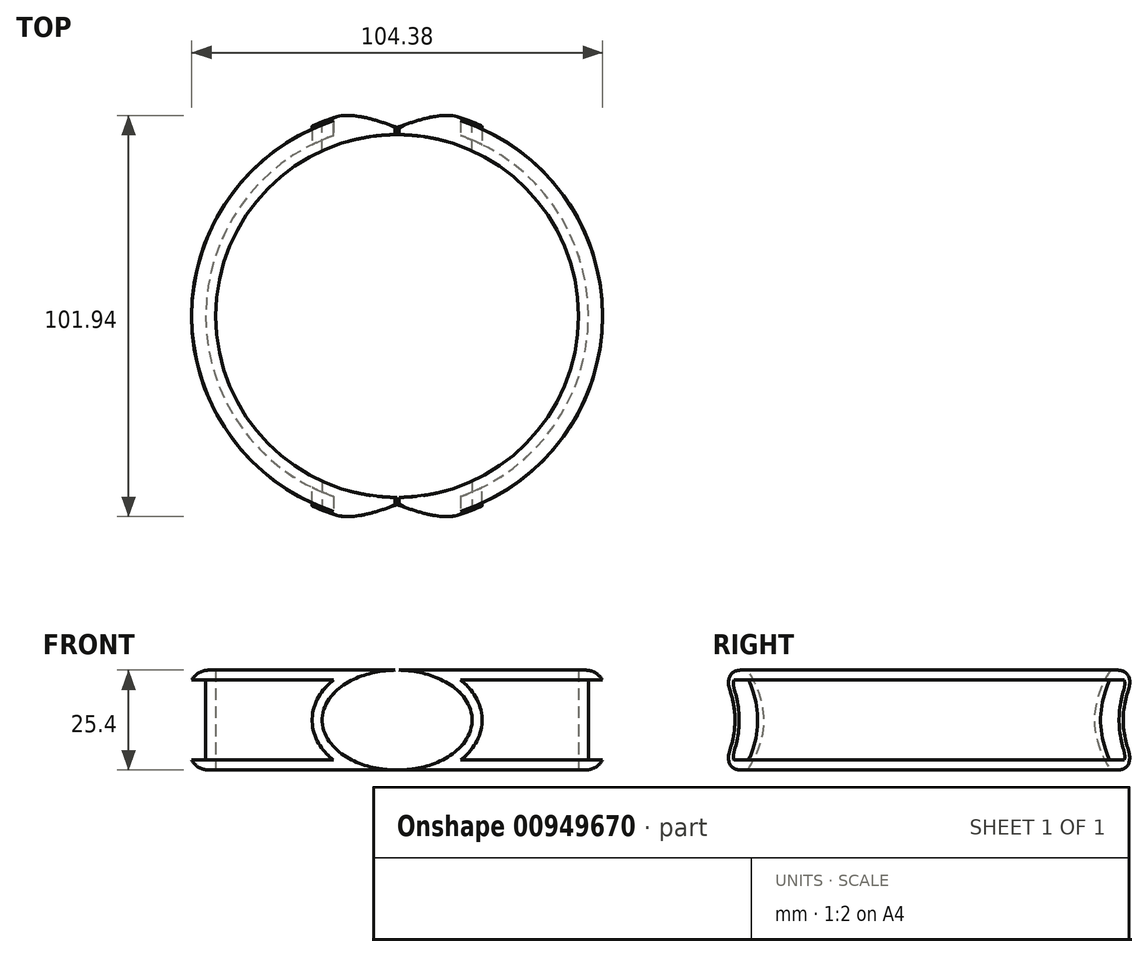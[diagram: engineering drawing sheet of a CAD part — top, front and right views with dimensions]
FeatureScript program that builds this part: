
annotation { "Feature Type Name" : "Feature", "Feature Type Description" : "" }
export const myFeature = defineFeature(function(context is Context, id is Id, definition is map)
    precondition{}
    {
        {
            var Q0;
            Q0=qCreatedBy(makeId("Top.planeOp"),FACE);
            var sketch = newSketch(context, id + "F0", { "sketchPlane" : qUnion([Q0])});
            skCircle(sketch, "E0", {"center": v(0, 0) * mm, "radius": 52.87 * mm});
            skCircle(sketch, "E1", {"center": v(0, 0) * mm, "radius": 46.07 * mm});
            skSolve(sketch);
        }
        {
            var Q0;
            Q0=makeQuery(id+"F0.imprint","IMPRINT",FACE,{"disambiguationData":[TD([[makeQuery(id+"F0.imprint","IMPRINT",EDGE,{"derivedFrom":sQuery(id+"F0.wireOp",EDGE,"E0")}),1.0]])]});
            extrude(context, id + "F1", {"entities" : qUnion([Q0]), "depth" : 25.4 * mm, "offsetDistance" : 25.4 * mm});
        }
        {
            var Q0;
            Q0=qCreatedBy(makeId("Front.planeOp"),FACE);
            var sketch = newSketch(context, id + "F2", { "sketchPlane" : qUnion([Q0])});
            skLineSegment(sketch, "E2", {"start": v(0, 0) * mm, "end": v(0, 25.4) * mm});
            skLineSegment(sketch, "E3", {"start": v(0, 25.4) * mm, "end": v(0, 12.7) * mm});
            skEllipse(sketch, "E4", {"center": v(0, 12.7) * mm, "majorRadius": 19.05 * mm, "minorRadius": 12.7 * mm, "majorAxis": v(1, 0)});
            skSolve(sketch);
        }
        {
            var Q0;
            {var subQ0=sQuery(id+"F2.wireOp",EDGE,"E2");Q0=makeQuery(id+"F2.imprint","IMPRINT",FACE,{"disambiguationData":[TD([[makeQuery(id+"F2.imprint","IMPRINT",EDGE,{"derivedFrom":subQ0}),1.0]])]});}
            var Q1;
            {var subQ0=sQuery(id+"F2.wireOp",EDGE,"E2");Q1=makeQuery(id+"F2.imprint","IMPRINT",FACE,{"disambiguationData":[TD([[makeQuery(id+"F2.imprint","IMPRINT",EDGE,{"derivedFrom":subQ0}),-1.0]])]});}
            var Q2;
            Q2=sQuery(id+"F2.wireOp",EDGE,"E4");
            extrude(context, id + "F3", {"entities" : qUnion([Q0, Q1]), "operationType" : NewBodyOperationType.REMOVE, "surfaceEntities" : qUnion([Q2]), "oppositeDirection" : true, "depth" : 127 * mm, "offsetDistance" : 25.4 * mm, "symmetric" : true});
        }
        {
            var Q0;
            Q0=makeQuery(id+"F3.boolean.opBoolean","SPLIT",FACE,{"disambiguationData":[OD(0.0)],"derivedFrom":makeQuery(id+"F1.opExtrude","SWEPT_FACE",FACE,{"disambiguationData":[OSD([sQuery(id+"F0.wireOp",EDGE,"E0")])]})});
            shell(context, id + "F4", {"entities" : qUnion([Q0]), "thickness" : 2.54 * mm});
        }
        {
            var Q0;
            Q0=makeQuery(id+"F3.boolean.opBoolean","SPLIT",FACE,{"disambiguationData":[OD(1.0)],"derivedFrom":makeQuery(id+"F1.opExtrude","SWEPT_FACE",FACE,{"disambiguationData":[OSD([sQuery(id+"F0.wireOp",EDGE,"E0")])]})});
            shell(context, id + "F5", {"entities" : qUnion([Q0]), "thickness" : 2.54 * mm});
        }
        {
            var Q0;
            Q0=makeQuery(id+"F3.boolean.opBoolean","SPLIT",EDGE,{"disambiguationData":[OD(0.0)],"derivedFrom":makeQuery(id+"F1.opExtrude","CAP_EDGE",EDGE,{"disambiguationData":[OSD([sQuery(id+"F0.wireOp",EDGE,"E0")])],"isStart":false})});
            var Q1;
            Q1=makeQuery(id+"F3.boolean.opBoolean","SPLIT",EDGE,{"disambiguationData":[OD(0.0)],"derivedFrom":makeQuery(id+"F1.opExtrude","CAP_EDGE",EDGE,{"disambiguationData":[OSD([sQuery(id+"F0.wireOp",EDGE,"E0")])],"isStart":true})});
            var Q2;
            Q2=makeQuery(id+"F3.boolean.opBoolean","SPLIT",EDGE,{"disambiguationData":[OD(1.0)],"derivedFrom":makeQuery(id+"F1.opExtrude","CAP_EDGE",EDGE,{"disambiguationData":[OSD([sQuery(id+"F0.wireOp",EDGE,"E0")])],"isStart":true})});
            var Q3;
            Q3=makeQuery(id+"F3.boolean.opBoolean","SPLIT",EDGE,{"disambiguationData":[OD(1.0)],"derivedFrom":makeQuery(id+"F1.opExtrude","CAP_EDGE",EDGE,{"disambiguationData":[OSD([sQuery(id+"F0.wireOp",EDGE,"E0")])],"isStart":false})});
            fillet(context, id + "F6", {"entities" : qUnion([Q0, Q1, Q2, Q3]), "radius" : 5.08 * mm, "tangentPropagation" : true, "allowEdgeOverflow" : false});
        }
    });
